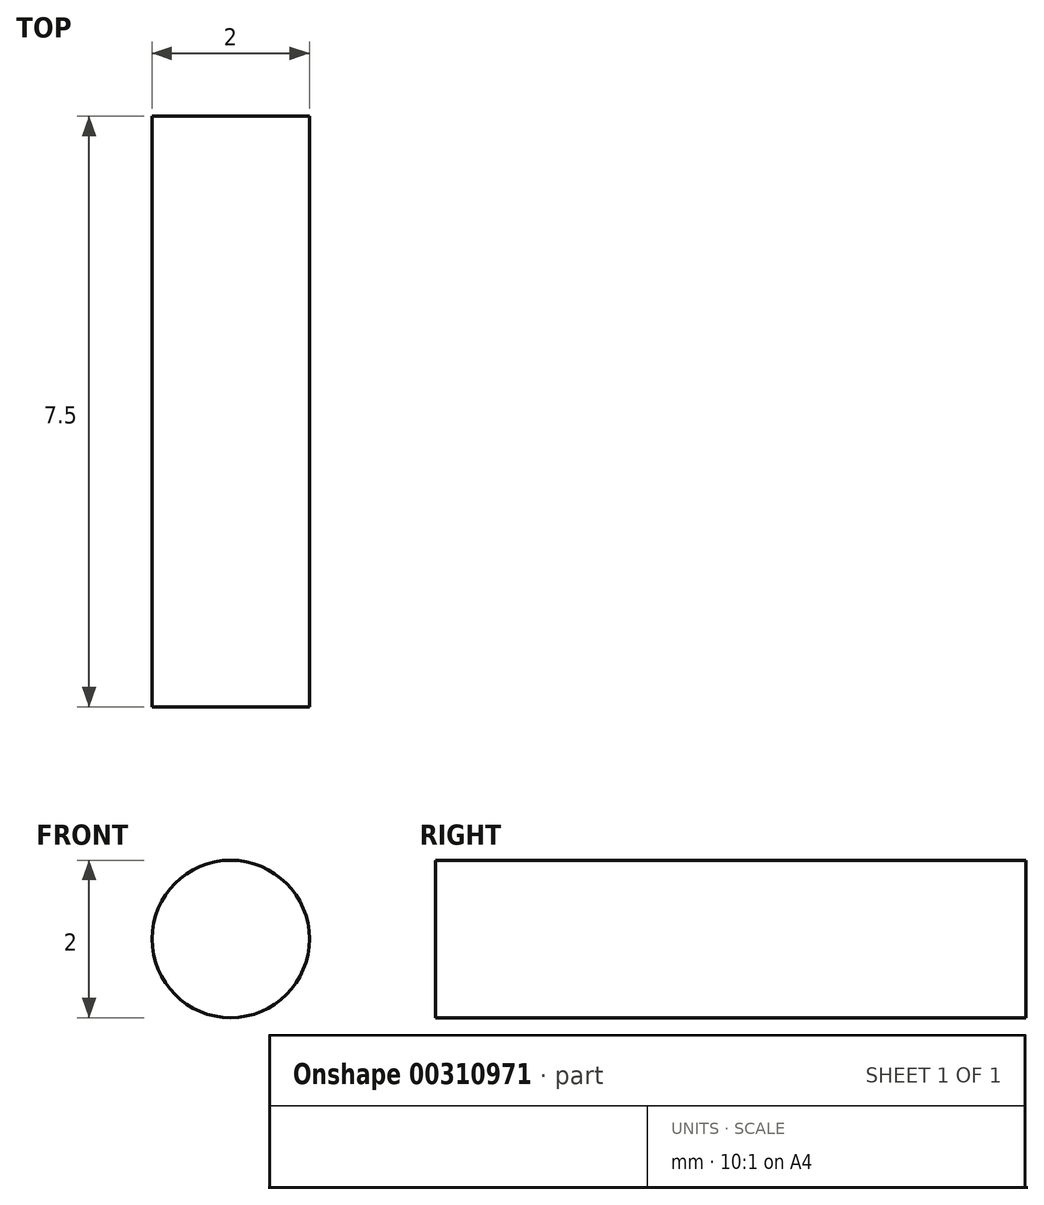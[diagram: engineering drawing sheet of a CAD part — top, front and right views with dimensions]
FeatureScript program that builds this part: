
annotation { "Feature Type Name" : "Feature", "Feature Type Description" : "" }
export const myFeature = defineFeature(function(context is Context, id is Id, definition is map)
    precondition{}
    {
        {
            var Q0;
            Q0=qCreatedBy(makeId("Front.planeOp"),FACE);
            var sketch = newSketch(context, id + "F0", { "sketchPlane" : qUnion([Q0])});
            skCircle(sketch, "E0", {"center": v(0, 0) * mm, "radius": 1 * mm});
            skSolve(sketch);
        }
        {
            var Q0;
            Q0=makeQuery(id+"F0.imprint","IMPRINT",FACE,{"disambiguationData":[TD([[makeQuery(id+"F0.imprint","IMPRINT",EDGE,{"derivedFrom":sQuery(id+"F0.wireOp",EDGE,"E0")}),1.0]])]});
            extrude(context, id + "F1", {"entities" : qUnion([Q0]), "depth" : 7.5 * mm});
        }
    });
